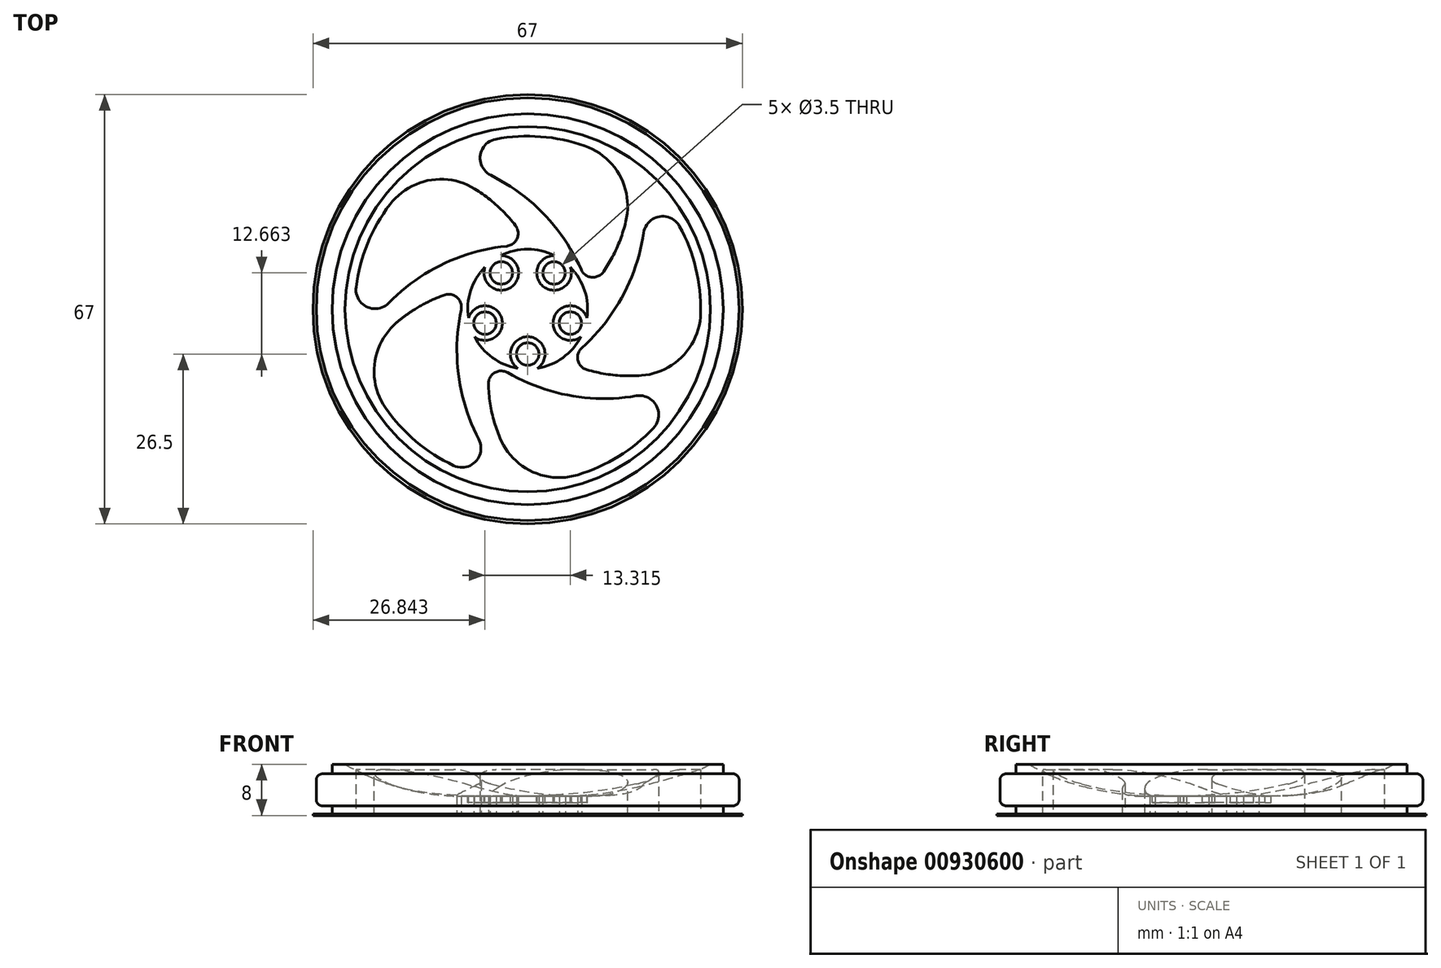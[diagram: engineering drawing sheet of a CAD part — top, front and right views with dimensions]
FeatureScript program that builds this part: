
annotation { "Feature Type Name" : "Feature", "Feature Type Description" : "" }
export const myFeature = defineFeature(function(context is Context, id is Id, definition is map)
    precondition{}
    {
        {
            var Q0;
            Q0=qCreatedBy(makeId("Front.planeOp"),FACE);
            var sketch = newSketch(context, id + "F0", { "sketchPlane" : qUnion([Q0])});
            skLineSegment(sketch, "E0.right", {"start": v(33, 1.5) * mm, "end": v(33, 6.5) * mm});
            skLineSegment(sketch, "E1", {"start": v(30.5, 6.5) * mm, "end": v(33, 6.5) * mm});
            skLineSegment(sketch, "E2", {"start": v(30.5, 6.5) * mm, "end": v(30.5, 8) * mm});
            skLineSegment(sketch, "E3.MirrorCS", {"start": v(30.5, 1.5) * mm, "end": v(30.5, 0) * mm});
            skLineSegment(sketch, "E4.MirrorCS", {"start": v(30.5, 1.5) * mm, "end": v(33, 1.5) * mm});
            skLineSegment(sketch, "E5.trimOffspring", {"start": v(28.5, 8) * mm, "end": v(30.5, 8) * mm});
            skLineSegment(sketch, "E6", {"start": v(0, 0) * mm, "end": v(30.5, 0) * mm});
            skLineSegment(sketch, "E7", {"start": v(0, 0) * mm, "end": v(0, 3) * mm});
            skLineSegment(sketch, "E8", {"start": v(0, 3) * mm, "end": v(10, 3) * mm});
            skArc(sketch, "E9", {"start": v(10, 3) * mm, "mid": v(19.58, 4.27) * mm, "end": v(28.5, 8) * mm});
            skSolve(sketch);
        }
        {
            var Q0;
            Q0=qSketchRegion(id+"F0",true);
            var Q1;
            Q1=sQuery(id+"F0.wireOp",EDGE,"E7");
            revolve(context, id + "F1", {"entities" : qUnion([Q0]), "axis" : qUnion([Q1]), "revolveType" : RevolveType.FULL});
        }
        {
            var Q0;
            Q0=makeQuery(id+"F1.opRevolve","SWEPT_EDGE",EDGE,{"disambiguationData":[OSD([sQuery(id+"F0.wireOp",EDGE,"E0.right"),sQuery(id+"F0.wireOp",EDGE,"E1")])]});
            var Q1;
            Q1=makeQuery(id+"F1.opRevolve","SWEPT_EDGE",EDGE,{"disambiguationData":[OSD([sQuery(id+"F0.wireOp",EDGE,"E0.right"),sQuery(id+"F0.wireOp",EDGE,"E4.MirrorCS")])]});
            fillet(context, id + "F2", {"entities" : qUnion([Q0, Q1]), "radius" : 1 * mm, "tangentPropagation" : true, "allowEdgeOverflow" : false});
        }
        {
            var Q0;
            Q0=makeQuery(id+"F1.opRevolve","SWEPT_FACE",FACE,{"disambiguationData":[OSD([sQuery(id+"F0.wireOp",EDGE,"E6")])]});
            var sketch = newSketch(context, id + "F3", { "sketchPlane" : qUnion([Q0])});
            skCircle(sketch, "E10", {"center": v(0, 0) * mm, "radius": 10 * mm, "construction": true});
            skCircle(sketch, "E11", {"center": v(0, 0) * mm, "radius": 28.5 * mm, "construction": true});
            skArc(sketch, "E12", {"start": v(-3, 26.83) * mm, "mid": v(-17.06, 20.93) * mm, "end": v(-25.68, 8.34) * mm});
            skArc(sketch, "E13.trimOffspring", {"start": v(-26.45, 5.44) * mm, "mid": v(-25.18, -9.76) * mm, "end": v(-15.87, -21.84) * mm});
            skArc(sketch, "E14.trimOffspring", {"start": v(18.2, -19.95) * mm, "mid": v(26.1, -6.9) * mm, "end": v(25.68, 8.34) * mm});
            skLineSegment(sketch, "E15", {"start": v(0, 28.5) * mm, "end": v(0, 0) * mm, "construction": true});
            skLineSegment(sketch, "E16", {"start": v(0, 0) * mm, "end": v(-25.68, 8.34) * mm, "construction": true});
            skLineSegment(sketch, "E17", {"start": v(0, 0) * mm, "end": v(25.68, 8.34) * mm, "construction": true});
            skLineSegment(sketch, "E18", {"start": v(0, 0) * mm, "end": v(-15.87, -21.84) * mm, "construction": true});
            skLineSegment(sketch, "E19", {"start": v(0, 0) * mm, "end": v(15.87, -21.84) * mm, "construction": true});
            skArc(sketch, "E20.trimOffspring", {"start": v(24.6, 11.14) * mm, "mid": v(14.63, 22.7) * mm, "end": v(0, 27) * mm});
            skArc(sketch, "E21.trimOffspring", {"start": v(-13.35, -23.47) * mm, "mid": v(1.5, -26.96) * mm, "end": v(15.87, -21.84) * mm});
            skCircle(sketch, "E22", {"center": v(0, 7) * mm, "radius": 1.75 * mm});
            skCircle(sketch, "E23", {"center": v(-4.11, -5.66) * mm, "radius": 1.75 * mm});
            skCircle(sketch, "E24", {"center": v(4.11, -5.66) * mm, "radius": 1.75 * mm});
            skCircle(sketch, "E25", {"center": v(6.66, 2.16) * mm, "radius": 1.75 * mm});
            skCircle(sketch, "E26", {"center": v(-6.66, 2.16) * mm, "radius": 1.75 * mm});
            skArc(sketch, "E27", {"start": v(-3, 26.83) * mm, "mid": v(-10.37, 12.71) * mm, "end": v(-9.48, -3.2) * mm});
            skArc(sketch, "E28", {"start": v(-26.45, 5.44) * mm, "mid": v(-15.3, -5.93) * mm, "end": v(0.1, -10) * mm});
            skArc(sketch, "E29", {"start": v(-13.35, -23.47) * mm, "mid": v(0.92, -16.38) * mm, "end": v(9.54, -2.99) * mm});
            skArc(sketch, "E30", {"start": v(18.2, -19.95) * mm, "mid": v(15.86, -4.19) * mm, "end": v(5.8, 8.15) * mm});
            skArc(sketch, "E31", {"start": v(24.6, 11.14) * mm, "mid": v(8.89, 13.8) * mm, "end": v(-5.96, 8.03) * mm});
            skArc(sketch, "E32", {"start": v(0, 27) * mm, "mid": v(-5.04, 18.16) * mm, "end": v(-5.96, 8.03) * mm});
            skArc(sketch, "E33", {"start": v(-25.68, 8.34) * mm, "mid": v(-18.83, 0.82) * mm, "end": v(-9.48, -3.2) * mm});
            skArc(sketch, "E34", {"start": v(-15.87, -21.84) * mm, "mid": v(-6.6, -17.65) * mm, "end": v(0.1, -10) * mm});
            skArc(sketch, "E35", {"start": v(15.87, -21.84) * mm, "mid": v(14.75, -11.73) * mm, "end": v(9.54, -2.99) * mm});
            skArc(sketch, "E36", {"start": v(25.68, 8.34) * mm, "mid": v(15.71, 10.4) * mm, "end": v(5.8, 8.15) * mm});
            skSolve(sketch);
        }
        {
            var Q0;
            Q0=qSketchRegion(id+"F3",true);
            extrude(context, id + "F4", {"entities" : qUnion([Q0]), "operationType" : NewBodyOperationType.REMOVE, "oppositeDirection" : true, "depth" : 25 * mm});
        }
        {
            var Q0;
            Q0=makeQuery(id+"F4.boolean.opBoolean","COPY",EDGE,{"derivedFrom":makeQuery(id+"F4.opExtrude","SWEPT_EDGE",EDGE,{"disambiguationData":[OSD([sQuery(id+"F3.wireOp",EDGE,"E12"),sQuery(id+"F3.wireOp",EDGE,"E27")])]})});
            var Q1;
            Q1=makeQuery(id+"F4.boolean.opBoolean","COPY",EDGE,{"derivedFrom":makeQuery(id+"F4.opExtrude","SWEPT_EDGE",EDGE,{"disambiguationData":[OSD([sQuery(id+"F3.wireOp",EDGE,"E20.trimOffspring"),sQuery(id+"F3.wireOp",EDGE,"E31")])]})});
            var Q2;
            Q2=makeQuery(id+"F4.boolean.opBoolean","COPY",EDGE,{"derivedFrom":makeQuery(id+"F4.opExtrude","SWEPT_EDGE",EDGE,{"disambiguationData":[OSD([sQuery(id+"F3.wireOp",EDGE,"E14.trimOffspring"),sQuery(id+"F3.wireOp",EDGE,"E30")])]})});
            var Q3;
            Q3=makeQuery(id+"F4.boolean.opBoolean","COPY",EDGE,{"derivedFrom":makeQuery(id+"F4.opExtrude","SWEPT_EDGE",EDGE,{"disambiguationData":[OSD([sQuery(id+"F3.wireOp",EDGE,"E21.trimOffspring"),sQuery(id+"F3.wireOp",EDGE,"E29")])]})});
            var Q4;
            Q4=makeQuery(id+"F4.boolean.opBoolean","COPY",EDGE,{"derivedFrom":makeQuery(id+"F4.opExtrude","SWEPT_EDGE",EDGE,{"disambiguationData":[OSD([sQuery(id+"F3.wireOp",EDGE,"E13.trimOffspring"),sQuery(id+"F3.wireOp",EDGE,"E28")])]})});
            fillet(context, id + "F5", {"entities" : qUnion([Q0, Q1, Q2, Q3, Q4]), "radius" : 3 * mm, "tangentPropagation" : true, "allowEdgeOverflow" : false});
        }
        {
            var Q0;
            Q0=makeQuery(id+"F4.boolean.opBoolean","COPY",EDGE,{"derivedFrom":makeQuery(id+"F4.opExtrude","SWEPT_EDGE",EDGE,{"disambiguationData":[OSD([sQuery(id+"F3.wireOp",EDGE,"E14.trimOffspring"),sQuery(id+"F3.wireOp",EDGE,"lH133nUo-b4dK-7Uis-ALbx-UH7YrD5dzAr5")])]})});
            var Q1;
            Q1=makeQuery(id+"F4.boolean.opBoolean","COPY",EDGE,{"derivedFrom":makeQuery(id+"F4.opExtrude","SWEPT_EDGE",EDGE,{"disambiguationData":[OSD([sQuery(id+"F3.wireOp",EDGE,"E20.trimOffspring"),sQuery(id+"F3.wireOp",EDGE,"Y5TeA7qx-hglw-YKO1-yJVa-Mu3tWydujS0s")])]})});
            var Q2;
            Q2=makeQuery(id+"F4.boolean.opBoolean","COPY",EDGE,{"derivedFrom":makeQuery(id+"F4.opExtrude","SWEPT_EDGE",EDGE,{"disambiguationData":[OSD([sQuery(id+"F3.wireOp",EDGE,"E12"),sQuery(id+"F3.wireOp",EDGE,"K8Gechwi-EIRI-6laA-ybGk-XkUKvmpAPVkA")])]})});
            var Q3;
            Q3=makeQuery(id+"F4.boolean.opBoolean","COPY",EDGE,{"derivedFrom":makeQuery(id+"F4.opExtrude","SWEPT_EDGE",EDGE,{"disambiguationData":[OSD([sQuery(id+"F3.wireOp",EDGE,"E13.trimOffspring"),sQuery(id+"F3.wireOp",EDGE,"yrZSpx71-NN5u-So2I-DmkD-7K2vPXZf8bNT")])]})});
            var Q4;
            Q4=makeQuery(id+"F4.boolean.opBoolean","COPY",EDGE,{"derivedFrom":makeQuery(id+"F4.opExtrude","SWEPT_EDGE",EDGE,{"disambiguationData":[OSD([sQuery(id+"F3.wireOp",EDGE,"E21.trimOffspring"),sQuery(id+"F3.wireOp",EDGE,"3wq5JMd6-PSVr-Z4Na-BiTl-nTZF3QSmccvR")])]})});
            fillet(context, id + "F6", {"entities" : qUnion([Q0, Q1, Q2, Q3, Q4]), "radius" : 10 * mm, "tangentPropagation" : true, "allowEdgeOverflow" : false});
        }
        {
            var Q0;
            Q0=makeQuery(id+"F4.boolean.opBoolean","COPY",EDGE,{"derivedFrom":makeQuery(id+"F4.opExtrude","SWEPT_EDGE",EDGE,{"disambiguationData":[OSD([sQuery(id+"F3.wireOp",EDGE,"E28"),sQuery(id+"F3.wireOp",EDGE,"E34")])]})});
            var Q1;
            Q1=makeQuery(id+"F4.boolean.opBoolean","COPY",EDGE,{"derivedFrom":makeQuery(id+"F4.opExtrude","SWEPT_EDGE",EDGE,{"disambiguationData":[OSD([sQuery(id+"F3.wireOp",EDGE,"E29"),sQuery(id+"F3.wireOp",EDGE,"E35")])]})});
            var Q2;
            Q2=makeQuery(id+"F4.boolean.opBoolean","COPY",EDGE,{"derivedFrom":makeQuery(id+"F4.opExtrude","SWEPT_EDGE",EDGE,{"disambiguationData":[OSD([sQuery(id+"F3.wireOp",EDGE,"E30"),sQuery(id+"F3.wireOp",EDGE,"E36")])]})});
            var Q3;
            Q3=makeQuery(id+"F4.boolean.opBoolean","COPY",EDGE,{"derivedFrom":makeQuery(id+"F4.opExtrude","SWEPT_EDGE",EDGE,{"disambiguationData":[OSD([sQuery(id+"F3.wireOp",EDGE,"E31"),sQuery(id+"F3.wireOp",EDGE,"E32")])]})});
            var Q4;
            Q4=makeQuery(id+"F4.boolean.opBoolean","COPY",EDGE,{"derivedFrom":makeQuery(id+"F4.opExtrude","SWEPT_EDGE",EDGE,{"disambiguationData":[OSD([sQuery(id+"F3.wireOp",EDGE,"E27"),sQuery(id+"F3.wireOp",EDGE,"E33")])]})});
            fillet(context, id + "F7", {"entities" : qUnion([Q0, Q1, Q2, Q3, Q4]), "radius" : 2 * mm, "tangentPropagation" : true, "allowEdgeOverflow" : false});
        }
        {
            var Q0;
            Q0=makeQuery(id+"F1.opRevolve","SWEPT_FACE",FACE,{"disambiguationData":[OSD([sQuery(id+"F0.wireOp",EDGE,"E8")])]});
            var sketch = newSketch(context, id + "F8", { "sketchPlane" : qUnion([Q0])});
            skArc(sketch, "E37", {"start": v(-6.66, 6.56) * mm, "mid": v(-2.53, 3.48) * mm, "end": v(-4.18, 8.36) * mm});
            skArc(sketch, "E38", {"start": v(4.18, 8.36) * mm, "mid": v(2.53, 3.48) * mm, "end": v(6.66, 6.56) * mm});
            skArc(sketch, "E39", {"start": v(9.25, -1.4) * mm, "mid": v(4.09, -1.33) * mm, "end": v(8.3, -4.3) * mm});
            skArc(sketch, "E40", {"start": v(1.53, -9.22) * mm, "mid": v(0, -4.3) * mm, "end": v(-1.53, -9.22) * mm});
            skArc(sketch, "E41", {"start": v(-8.3, -4.3) * mm, "mid": v(-4.09, -1.33) * mm, "end": v(-9.25, -1.4) * mm});
            skArc(sketch, "E42", {"start": v(-6.66, 6.56) * mm, "mid": v(-8.9, 2.89) * mm, "end": v(-9.25, -1.4) * mm});
            skArc(sketch, "E43.trimOffspring", {"start": v(4.18, 8.36) * mm, "mid": v(0, 9.35) * mm, "end": v(-4.18, 8.36) * mm});
            skArc(sketch, "E44.trimOffspring", {"start": v(9.25, -1.4) * mm, "mid": v(8.9, 2.89) * mm, "end": v(6.66, 6.56) * mm});
            skArc(sketch, "E45.trimOffspring", {"start": v(1.53, -9.22) * mm, "mid": v(5.5, -7.56) * mm, "end": v(8.3, -4.3) * mm});
            skArc(sketch, "E46.trimOffspring", {"start": v(-8.3, -4.3) * mm, "mid": v(-5.5, -7.56) * mm, "end": v(-1.53, -9.22) * mm});
            skSolve(sketch);
        }
        {
            var Q0;
            Q0=qSketchRegion(id+"F8",true);
            extrude(context, id + "F9", {"entities" : qUnion([Q0]), "operationType" : NewBodyOperationType.REMOVE, "oppositeDirection" : true, "depth" : 1 * mm});
        }
        {
            var Q0;
            Q0=makeQuery(id+"F1.opRevolve","SWEPT_FACE",FACE,{"disambiguationData":[OSD([sQuery(id+"F0.wireOp",EDGE,"E6")])]});
            var sketch = newSketch(context, id + "F10", { "sketchPlane" : qUnion([Q0])});
            skCircle(sketch, "E47", {"center": v(0, 0) * mm, "radius": 33.5 * mm});
            skCircle(sketch, "E48", {"center": v(0, 0) * mm, "radius": 30.5 * mm});
            skSolve(sketch);
        }
        {
            var Q0;
            Q0=qSketchRegion(id+"F10",true);
            extrude(context, id + "F11", {"entities" : qUnion([Q0]), "operationType" : NewBodyOperationType.ADD, "oppositeDirection" : true, "depth" : 0.2 * mm, "offsetDistance" : 25 * mm});
        }
    });
